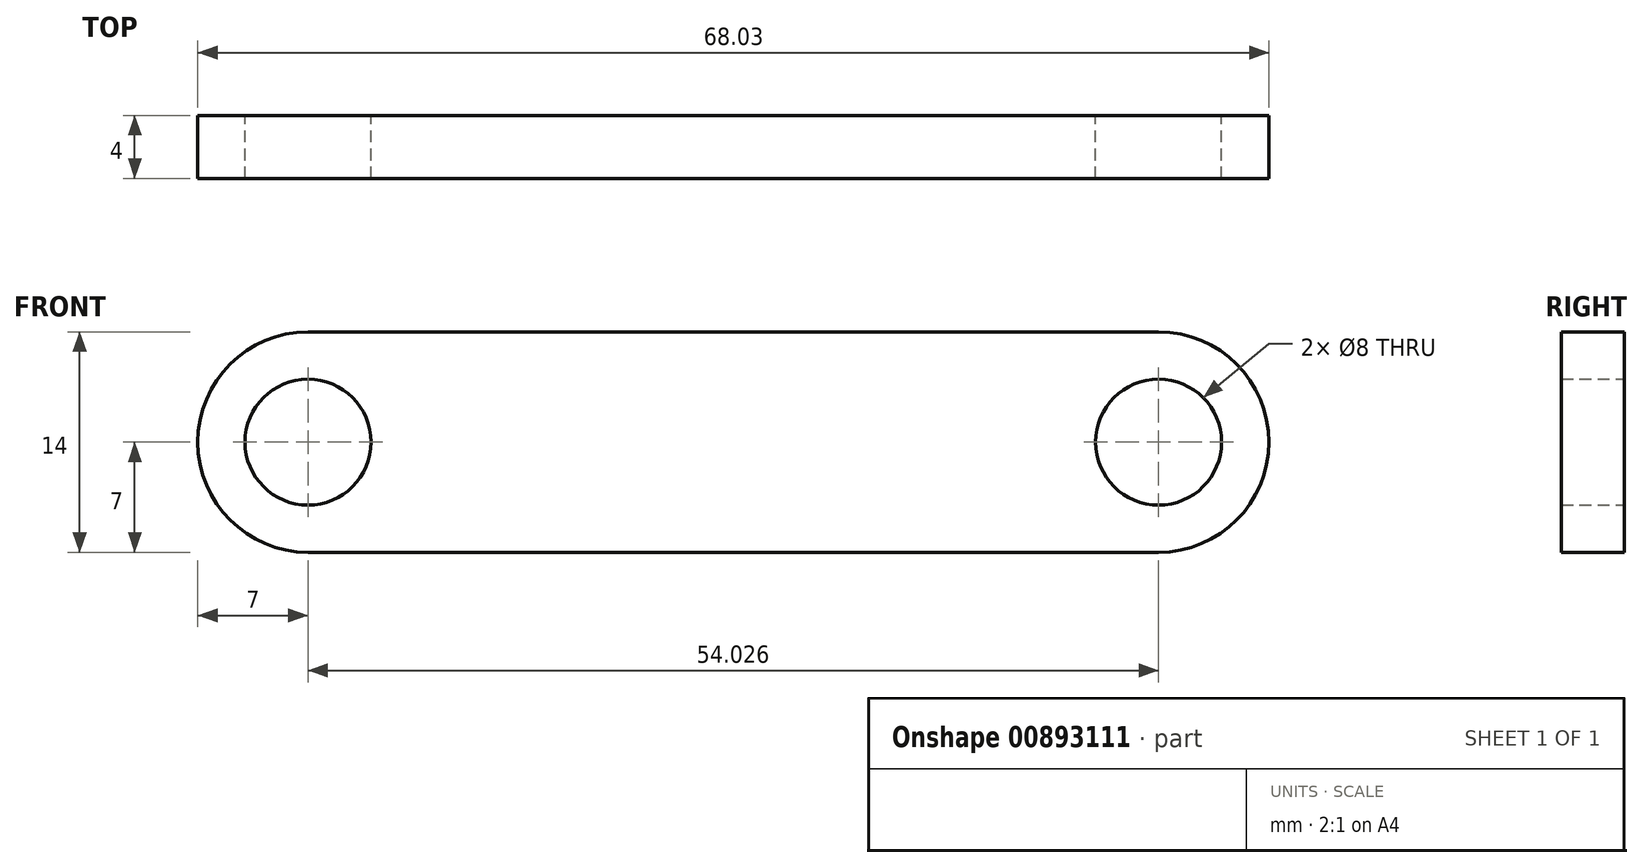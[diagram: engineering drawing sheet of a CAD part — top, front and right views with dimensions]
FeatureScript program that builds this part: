
annotation { "Feature Type Name" : "Feature", "Feature Type Description" : "" }
export const myFeature = defineFeature(function(context is Context, id is Id, definition is map)
    precondition{}
    {
        {
            assignVariable(context, id + "F0", {"name" : "Thickness", "anyValue" : 4});
        }
        {
            var Q0;
            Q0=qCreatedBy(makeId("Front.planeOp"),FACE);
            var sketch = newSketch(context, id + "F1", { "sketchPlane" : qUnion([Q0])});
            skCircle(sketch, "E0", {"center": v(0, 0) * mm, "radius": 4 * mm});
            skCircle(sketch, "E1", {"center": v(54.03, 0) * mm, "radius": 4 * mm});
            skArc(sketch, "E2", {"start": v(54.03, -7) * mm, "mid": v(61.03, 0) * mm, "end": v(54.03, 7) * mm});
            skArc(sketch, "E3", {"start": v(0, 7) * mm, "mid": v(-7, 0) * mm, "end": v(0, -7) * mm});
            skLineSegment(sketch, "E4", {"start": v(0, 7) * mm, "end": v(54.03, 7) * mm});
            skLineSegment(sketch, "E5", {"start": v(0, -7) * mm, "end": v(54.03, -7) * mm});
            skSolve(sketch);
        }
        {
            var Q0;
            Q0=makeQuery(id+"F1.imprint","IMPRINT",FACE,{"disambiguationData":[TD([[makeQuery(id+"F1.imprint","IMPRINT",EDGE,{"derivedFrom":sQuery(id+"F1.wireOp",EDGE,"E0")}),-1.0]])]});
            extrude(context, id + "F2", {"entities" : qUnion([Q0]), "depth" : (getVariable(context, 'Thickness')) * mm, "offsetDistance" : 25 * mm});
        }
    });
